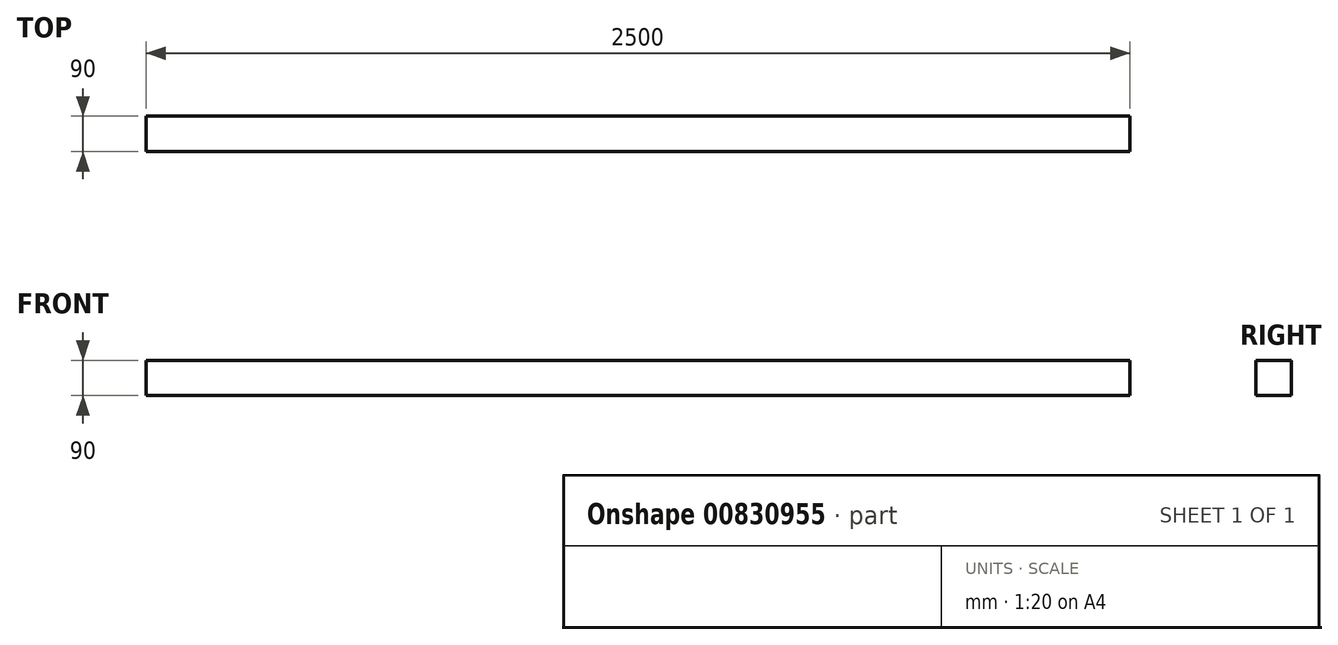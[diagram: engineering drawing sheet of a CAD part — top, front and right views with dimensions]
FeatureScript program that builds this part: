
annotation { "Feature Type Name" : "Feature", "Feature Type Description" : "" }
export const myFeature = defineFeature(function(context is Context, id is Id, definition is map)
    precondition{}
    {
        {
            var Q0;
            Q0=qCreatedBy(makeId("Right.planeOp"),FACE);
            var sketch = newSketch(context, id + "F0", { "sketchPlane" : qUnion([Q0])});
            skLineSegment(sketch, "E0.bottom", {"start": v(90, -90) * mm, "end": v(0, -90) * mm});
            skLineSegment(sketch, "E0.top", {"start": v(90, 0) * mm, "end": v(0, 0) * mm});
            skLineSegment(sketch, "E0.left", {"start": v(90, -90) * mm, "end": v(90, 0) * mm});
            skLineSegment(sketch, "E0.right", {"start": v(0, -90) * mm, "end": v(0, 0) * mm});
            skSolve(sketch);
        }
        {
            var Q0;
            Q0=makeQuery(id+"F0.imprint","IMPRINT",FACE,{"disambiguationData":[TD([[makeQuery(id+"F0.imprint","IMPRINT",EDGE,{"derivedFrom":sQuery(id+"F0.wireOp",EDGE,"E0.bottom")}),-1.0]])]});
            extrude(context, id + "F1", {"entities" : qUnion([Q0]), "depth" : 2500 * mm, "offsetDistance" : 25 * mm});
        }
    });
